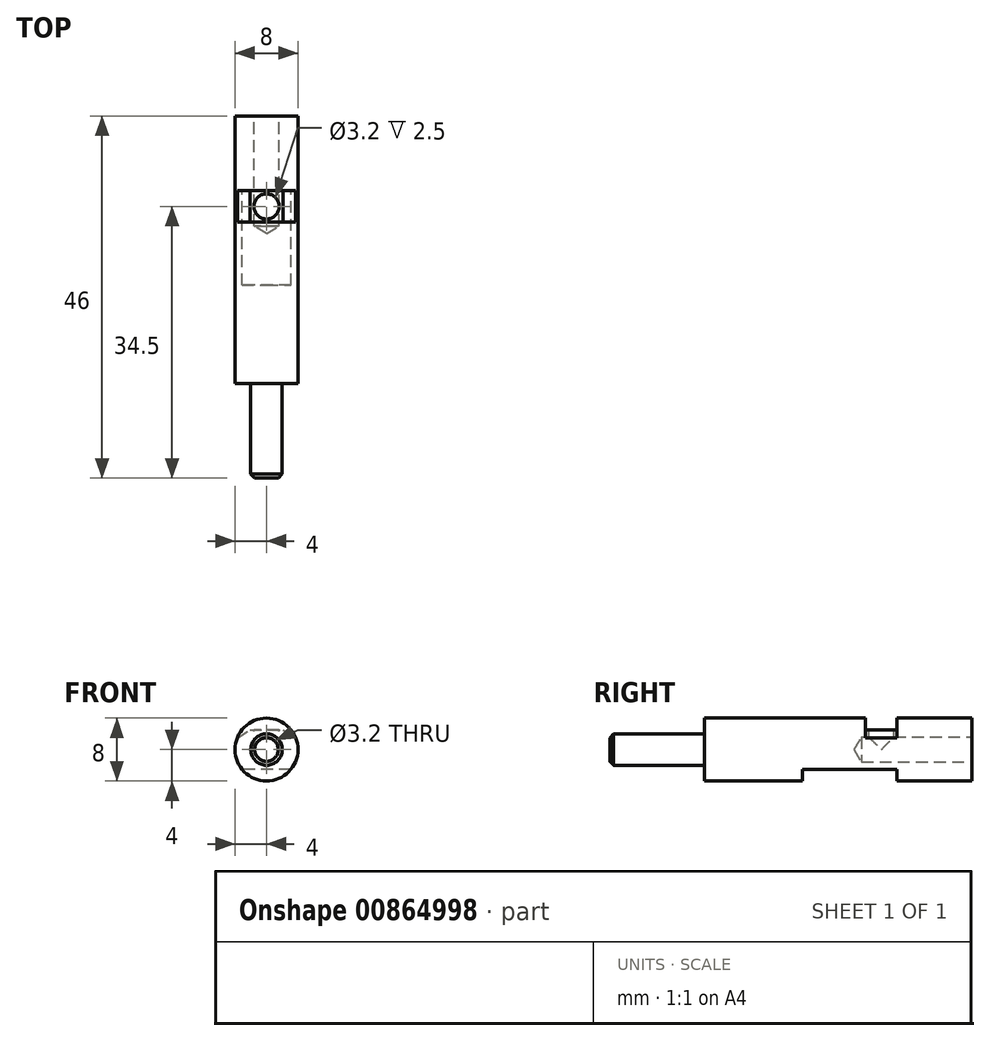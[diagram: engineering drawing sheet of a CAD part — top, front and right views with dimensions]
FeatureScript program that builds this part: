
annotation { "Feature Type Name" : "Feature", "Feature Type Description" : "" }
export const myFeature = defineFeature(function(context is Context, id is Id, definition is map)
    precondition{}
    {
        {
            var Q0;
            Q0=qCreatedBy(makeId("Front.planeOp"),FACE);
            var sketch = newSketch(context, id + "F0", { "sketchPlane" : qUnion([Q0])});
            skCircle(sketch, "E0", {"center": v(0, 0) * mm, "radius": 4 * mm});
            skCircle(sketch, "E1", {"center": v(0, 0) * mm, "radius": 2 * mm});
            skSolve(sketch);
        }
        {
            var Q0;
            Q0 = qSketchRegion(id + "F0", true);
            var Q1;
            Q1=makeQuery(id+"F0.imprint","IMPRINT",FACE,{"disambiguationData":[TD([[makeQuery(id+"F0.imprint","IMPRINT",EDGE,{"derivedFrom":sQuery(id+"F0.wireOp",EDGE,"E1")}),1.0]])]});
            extrude(context, id + "F1", {"entities" : qUnion([Q0, Q1]), "depth" : 34 * mm, "offsetDistance" : 25 * mm});
        }
        {
            var Q0;
            Q0=makeQuery(id+"F0.imprint","IMPRINT",FACE,{"disambiguationData":[TD([[makeQuery(id+"F0.imprint","IMPRINT",EDGE,{"derivedFrom":sQuery(id+"F0.wireOp",EDGE,"E1")}),1.0]])]});
            extrude(context, id + "F2", {"entities" : qUnion([Q0]), "operationType" : NewBodyOperationType.ADD, "depth" : 46 * mm, "offsetDistance" : 25 * mm});
        }
        {
            var Q0;
            Q0=qCreatedBy(makeId("Front.planeOp"),FACE);
            cPlane(context, id + "F3", {"entities" : qUnion([Q0]), "cplaneType" : CPlaneType.OFFSET, "offset" : 11.5 * mm, "width" : 150 * mm, "height" : 150 * mm});
        }
        {
            var Q0;
            Q0=makeQuery(id+"F2.opExtrude","CAP_EDGE",EDGE,{"disambiguationData":[OSD([sQuery(id+"F0.wireOp",EDGE,"E1")])],"isStart":false});
            chamfer(context, id + "F4", {"entities" : qUnion([Q0]), "width" : 0.5 * mm, "tangentPropagation" : true});
        }
        {
            var Q0;
            Q0=makeQuery(id+"F1.opExtrude","CAP_FACE",FACE,{"disambiguationData":[OSD([sQuery(id+"F0.wireOp",EDGE,"E0")])],"isStart":true});
            var sketch = newSketch(context, id + "F5", { "sketchPlane" : qUnion([Q0])});
            skPoint(sketch, "E2", {"position": v(0, 0) * mm});
            skSolve(sketch);
        }
        {
            var Q0;
            Q0=sQuery(id+"F5.wireOp",VERTEX,"E2");
            var Q1;
            Q1=makeQuery(id+"F1.opExtrude","SWEPT_BODY",BODY,{"disambiguationData":[OSD([sQuery(id+"F0.wireOp",EDGE,"E0")])]});
            hole(context, id + "F6", {"style" : HoleStyle.SIMPLE, "endStyle" : HoleEndStyle.BLIND, "holeDiameter" : 3.2 * mm, "majorDiameter" : 4 * mm, "holeDepth" : 14 * mm, "isTappedThrough" : true, "tappedDepth" : 12.9 * mm, "tapClearance" : 3, "startFromSketch" : true, "locations" : qUnion([Q0]), "scope" : qUnion([Q1])});
        }
        {
            var Q0;
            Q0=qCreatedBy(id+"F3.planeOp",FACE);
            var sketch = newSketch(context, id + "F7", { "sketchPlane" : qUnion([Q0])});
            skLineSegment(sketch, "E3.bottom", {"start": v(4, -4) * mm, "end": v(-4, -4) * mm});
            skLineSegment(sketch, "E3.top", {"start": v(4, -2.5) * mm, "end": v(-4, -2.5) * mm});
            skLineSegment(sketch, "E3.left", {"start": v(4, -4) * mm, "end": v(4, -2.5) * mm});
            skLineSegment(sketch, "E3.right", {"start": v(-4, -4) * mm, "end": v(-4, -2.5) * mm});
            skPoint(sketch, "E3.middle", {"position": v(0, -3.25) * mm});
            skLineSegment(sketch, "E4", {"start": v(-3.7, 1.5) * mm, "end": v(-2.1, 2.5) * mm});
            skLineSegment(sketch, "E5", {"start": v(-2.1, 2.5) * mm, "end": v(2.1, 2.5) * mm});
            skLineSegment(sketch, "E6", {"start": v(2.1, 2.5) * mm, "end": v(3.7, 1.5) * mm});
            skLineSegment(sketch, "E7", {"start": v(3.7, 1.5) * mm, "end": v(3.7, 4) * mm});
            skLineSegment(sketch, "E8", {"start": v(3.7, 4) * mm, "end": v(-3.7, 4) * mm});
            skLineSegment(sketch, "E9", {"start": v(-3.7, 4) * mm, "end": v(-3.7, 1.5) * mm});
            skCircle(sketch, "E10.0", {"center": v(0, 0) * mm, "radius": 1.6 * mm, "construction": true});
            skLineSegment(sketch, "E11", {"start": v(-1.6, 0) * mm, "end": v(-1.6, 2.5) * mm, "construction": true});
            skSolve(sketch);
        }
        {
            var Q0;
            Q0=makeQuery(id+"F7.imprint","IMPRINT",FACE,{"disambiguationData":[TD([[makeQuery(id+"F7.imprint","IMPRINT",EDGE,{"derivedFrom":sQuery(id+"F7.wireOp",EDGE,"E4")}),1.0]])]});
            extrude(context, id + "F8", {"entities" : qUnion([Q0]), "operationType" : NewBodyOperationType.REMOVE, "endBound" : BoundingType.SYMMETRIC, "oppositeDirection" : true, "depth" : 4 * mm, "offsetDistance" : 25 * mm});
        }
        {
            var Q0;
            Q0=makeQuery(id+"F7.imprint","IMPRINT",FACE,{"disambiguationData":[TD([[makeQuery(id+"F7.imprint","IMPRINT",EDGE,{"derivedFrom":sQuery(id+"F7.wireOp",EDGE,"E3.bottom")}),-1.0]])]});
            extrude(context, id + "F9", {"entities" : qUnion([Q0]), "operationType" : NewBodyOperationType.REMOVE, "depth" : 10 * mm, "offsetDistance" : 25 * mm, "hasSecondDirection" : true, "secondDirectionOppositeDirection" : true, "secondDirectionDepth" : 2 * mm});
        }
        {
            var Q0;
            Q0=makeQuery(id+"F8.boolean.opBoolean","COPY",FACE,{"derivedFrom":makeQuery(id+"F8.opExtrude","SWEPT_FACE",FACE,{"disambiguationData":[OSD([sQuery(id+"F7.wireOp",EDGE,"E5")])]})});
            var sketch = newSketch(context, id + "F10", { "sketchPlane" : qUnion([Q0])});
            skCircle(sketch, "E12", {"center": v(0, -11.5) * mm, "radius": 1.6 * mm});
            skSolve(sketch);
        }
        {
            var Q0;
            Q0 = qSketchRegion(id + "F10", true);
            extrude(context, id + "F11", {"entities" : qUnion([Q0]), "operationType" : NewBodyOperationType.REMOVE, "endBound" : BoundingType.UP_TO_NEXT, "oppositeDirection" : true, "depth" : 25 * mm, "offsetDistance" : 25 * mm});
        }
    });
